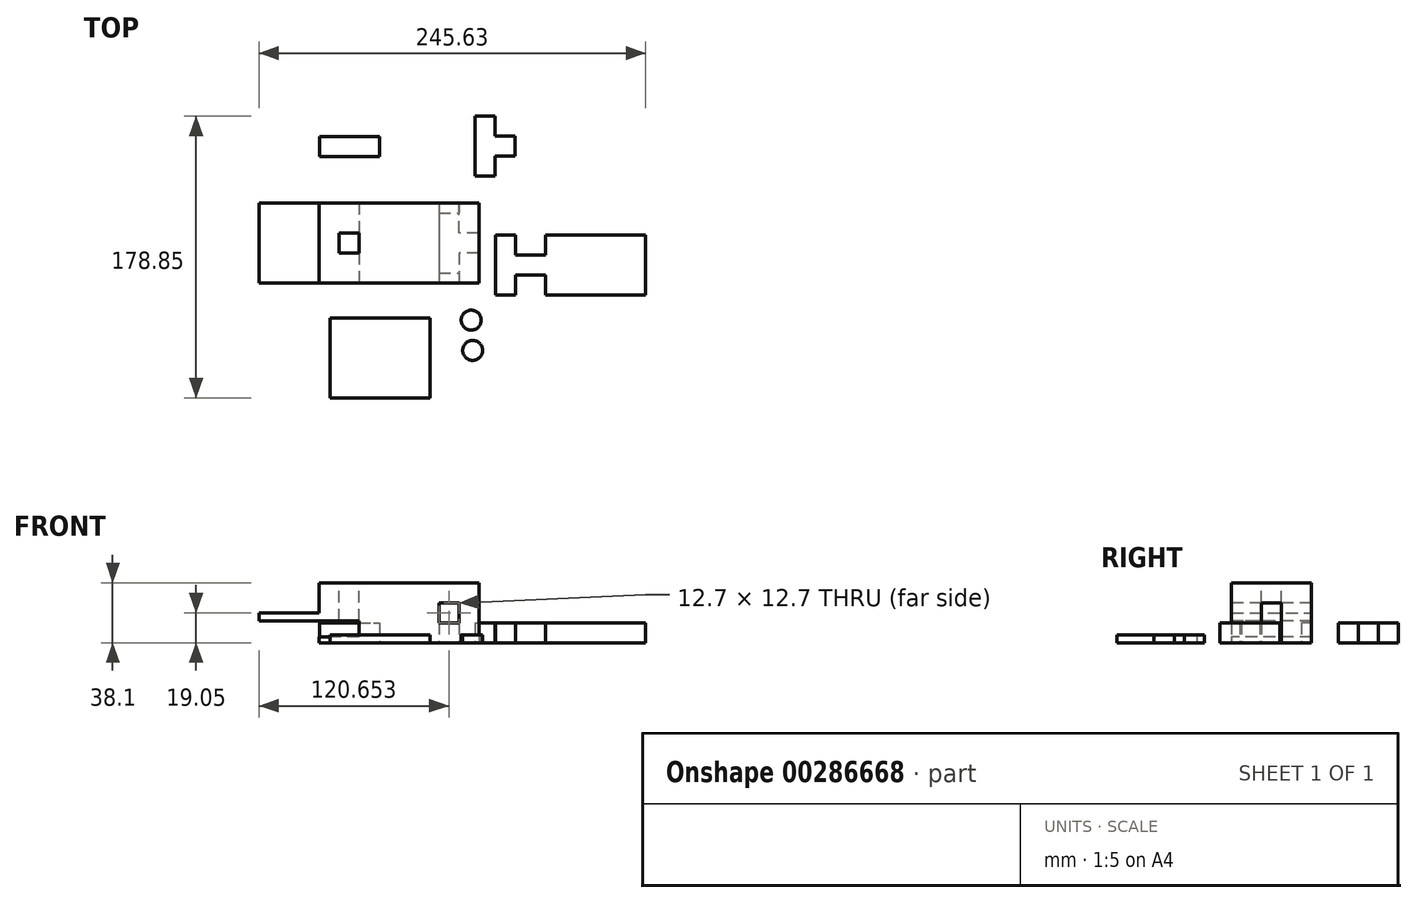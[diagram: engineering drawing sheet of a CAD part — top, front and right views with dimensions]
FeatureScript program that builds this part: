
annotation { "Feature Type Name" : "Feature", "Feature Type Description" : "" }
export const myFeature = defineFeature(function(context is Context, id is Id, definition is map)
    precondition{}
    {
        {
            var Q0;
            Q0=qCreatedBy(makeId("Top.planeOp"),FACE);
            var sketch = newSketch(context, id + "F0", { "sketchPlane" : qUnion([Q0])});
            skLineSegment(sketch, "E0", {"start": v(-57.42, 32.96) * mm, "end": v(44.18, 32.96) * mm});
            skLineSegment(sketch, "E1", {"start": v(-57.42, 32.96) * mm, "end": v(-57.42, -17.84) * mm});
            skLineSegment(sketch, "E2", {"start": v(-57.42, -17.84) * mm, "end": v(44.18, -17.84) * mm});
            skLineSegment(sketch, "E3", {"start": v(44.18, -17.84) * mm, "end": v(44.18, 32.96) * mm});
            skSolve(sketch);
        }
        {
            var Q0;
            Q0=makeQuery(id+"F0.imprint","IMPRINT",FACE,{"disambiguationData":[TD([[makeQuery(id+"F0.imprint","IMPRINT",EDGE,{"derivedFrom":sQuery(id+"F0.wireOp",EDGE,"E0")}),-1.0]])]});
            extrude(context, id + "F1", {"entities" : qUnion([Q0]), "depth" : 38.1 * mm});
        }
        {
            var Q0;
            Q0=makeQuery(id+"F1.opExtrude","SWEPT_FACE",FACE,{"disambiguationData":[OSD([sQuery(id+"F0.wireOp",EDGE,"E1")])]});
            var sketch = newSketch(context, id + "F2", { "sketchPlane" : qUnion([Q0])});
            skLineSegment(sketch, "E4", {"start": v(17.84, 19.05) * mm, "end": v(-32.96, 19.05) * mm});
            skLineSegment(sketch, "E5", {"start": v(-32.96, 19.05) * mm, "end": v(-32.96, 13.97) * mm});
            skLineSegment(sketch, "E6", {"start": v(-32.96, 13.97) * mm, "end": v(17.84, 13.97) * mm});
            skLineSegment(sketch, "E7", {"start": v(17.84, 19.05) * mm, "end": v(17.84, 13.97) * mm});
            skSolve(sketch);
        }
        {
            var Q0;
            Q0 = qSketchRegion(id + "F2", true);
            extrude(context, id + "F3", {"entities" : qUnion([Q0]), "operationType" : NewBodyOperationType.ADD, "depth" : 38.1 * mm});
        }
        {
            var Q0;
            Q0=makeQuery(id+"F1.opExtrude","CAP_FACE",FACE,{"disambiguationData":[OSD([sQuery(id+"F0.wireOp",EDGE,"E0"),sQuery(id+"F0.wireOp",EDGE,"E1"),sQuery(id+"F0.wireOp",EDGE,"E2"),sQuery(id+"F0.wireOp",EDGE,"E3")])],"isStart":true});
            var sketch = newSketch(context, id + "F4", { "sketchPlane" : qUnion([Q0])});
            skLineSegment(sketch, "E8", {"start": v(44.18, 17.84) * mm, "end": v(44.18, -1.2) * mm});
            skLineSegment(sketch, "E9", {"start": v(44.18, -32.96) * mm, "end": v(44.18, -13.9) * mm});
            skLineSegment(sketch, "E10", {"start": v(18.78, -1.2) * mm, "end": v(18.78, -13.9) * mm});
            skLineSegment(sketch, "E11", {"start": v(44.18, -1.2) * mm, "end": v(44.18, -13.9) * mm});
            skLineSegment(sketch, "E12", {"start": v(44.18, -1.2) * mm, "end": v(31.48, -1.2) * mm});
            skLineSegment(sketch, "E13", {"start": v(44.18, -13.9) * mm, "end": v(31.48, -13.9) * mm});
            skLineSegment(sketch, "E14", {"start": v(18.78, -13.9) * mm, "end": v(18.78, -26.6) * mm});
            skLineSegment(sketch, "E15", {"start": v(31.48, -13.9) * mm, "end": v(31.48, -26.6) * mm});
            skLineSegment(sketch, "E16", {"start": v(18.78, -26.6) * mm, "end": v(31.48, -26.6) * mm});
            skLineSegment(sketch, "E17", {"start": v(18.78, -1.2) * mm, "end": v(18.78, 11.5) * mm});
            skLineSegment(sketch, "E18", {"start": v(31.48, -1.2) * mm, "end": v(31.48, 11.5) * mm});
            skLineSegment(sketch, "E19", {"start": v(18.78, 11.5) * mm, "end": v(31.48, 11.5) * mm});
            skLineSegment(sketch, "E20", {"start": v(31.48, -1.2) * mm, "end": v(44.18, -1.2) * mm});
            skLineSegment(sketch, "E21", {"start": v(31.48, -13.9) * mm, "end": v(44.18, -13.9) * mm});
            skSolve(sketch);
        }
        {
            var Q0;
            Q0=makeQuery(id+"F4.imprint","IMPRINT",FACE,{"disambiguationData":[TD([[makeQuery(id+"F4.imprint","IMPRINT",EDGE,{"derivedFrom":sQuery(id+"F4.wireOp",EDGE,"E10")}),1.0]])]});
            extrude(context, id + "F5", {"entities" : qUnion([Q0]), "operationType" : NewBodyOperationType.REMOVE, "oppositeDirection" : true, "depth" : 25.4 * mm});
        }
        {
            var Q0;
            Q0=makeQuery(id+"F3.boolean.opBoolean","MERGE",FACE,{"derivedFrom":[makeQuery(id+"F1.opExtrude","SWEPT_FACE",FACE,{"disambiguationData":[OSD([sQuery(id+"F0.wireOp",EDGE,"E2")])]}),makeQuery(id+"F3.opExtrude","SWEPT_FACE",FACE,{"disambiguationData":[OSD([sQuery(id+"F2.wireOp",EDGE,"E7")])]})]});
            var sketch = newSketch(context, id + "F6", { "sketchPlane" : qUnion([Q0])});
            skLineSegment(sketch, "E22", {"start": v(44.18, 0) * mm, "end": v(31.48, 0) * mm});
            skLineSegment(sketch, "E23", {"start": v(31.48, 25.4) * mm, "end": v(18.78, 25.4) * mm});
            skLineSegment(sketch, "E24", {"start": v(18.78, 25.4) * mm, "end": v(18.78, 12.7) * mm});
            skLineSegment(sketch, "E25", {"start": v(18.78, 12.7) * mm, "end": v(31.48, 12.7) * mm});
            skLineSegment(sketch, "E26", {"start": v(31.48, 25.4) * mm, "end": v(31.48, 12.7) * mm});
            skSolve(sketch);
        }
        {
            var Q0;
            Q0 = qSketchRegion(id + "F6", true);
            extrude(context, id + "F7", {"entities" : qUnion([Q0]), "operationType" : NewBodyOperationType.REMOVE, "oppositeDirection" : true, "depth" : 254 * mm});
        }
        {
            var Q0;
            Q0=makeQuery(id+"F1.opExtrude","CAP_FACE",FACE,{"disambiguationData":[OSD([sQuery(id+"F0.wireOp",EDGE,"E0"),sQuery(id+"F0.wireOp",EDGE,"E1"),sQuery(id+"F0.wireOp",EDGE,"E2"),sQuery(id+"F0.wireOp",EDGE,"E3")])],"isStart":false});
            var sketch = newSketch(context, id + "F8", { "sketchPlane" : qUnion([Q0])});
            skLineSegment(sketch, "E27", {"start": v(-57.42, 32.96) * mm, "end": v(-57.42, -17.84) * mm});
            skLineSegment(sketch, "E28", {"start": v(-44.72, 7.56) * mm, "end": v(-44.72, 13.9) * mm});
            skLineSegment(sketch, "E29", {"start": v(-44.72, 7.56) * mm, "end": v(-44.72, 1.2) * mm});
            skLineSegment(sketch, "E30", {"start": v(-44.72, 1.2) * mm, "end": v(-32.02, 1.2) * mm});
            skLineSegment(sketch, "E31", {"start": v(-32.02, 1.2) * mm, "end": v(-32.02, 13.9) * mm});
            skLineSegment(sketch, "E32", {"start": v(-32.02, 13.9) * mm, "end": v(-44.72, 13.9) * mm});
            skSolve(sketch);
        }
        {
            var Q0;
            Q0=makeQuery(id+"F8.imprint","IMPRINT",FACE,{"disambiguationData":[TD([[makeQuery(id+"F8.imprint","IMPRINT",EDGE,{"derivedFrom":sQuery(id+"F8.wireOp",EDGE,"E28")}),-1.0]])]});
            extrude(context, id + "F9", {"entities" : qUnion([Q0]), "operationType" : NewBodyOperationType.REMOVE, "oppositeDirection" : true, "depth" : 31.75 * mm});
        }
        {
            var Q0;
            {var subQ1=sQuery(id+"F0.wireOp",EDGE,"E1");Q0=makeQuery(id+"F3.boolean.opBoolean","SPLIT",FACE,{"disambiguationData":[TD([makeQuery(id+"F3.opExtrude","SWEPT_FACE",FACE,{"disambiguationData":[OSD([sQuery(id+"F2.wireOp",EDGE,"E6")])]})])],"derivedFrom":makeQuery(id+"F1.opExtrude","SWEPT_FACE",FACE,{"disambiguationData":[OSD([subQ1])]})});}
            var sketch = newSketch(context, id + "F10", { "sketchPlane" : qUnion([Q0])});
            skLineSegment(sketch, "E33", {"start": v(17.84, 13.97) * mm, "end": v(17.84, 3.81) * mm});
            skLineSegment(sketch, "E34", {"start": v(-32.96, 13.97) * mm, "end": v(-32.96, 3.81) * mm});
            skLineSegment(sketch, "E35", {"start": v(-32.96, 3.81) * mm, "end": v(17.84, 3.81) * mm});
            skLineSegment(sketch, "E36", {"start": v(-32.96, 13.97) * mm, "end": v(17.84, 13.97) * mm});
            skSolve(sketch);
        }
        {
            var Q0;
            Q0=makeQuery(id+"F10.imprint","IMPRINT",FACE,{"disambiguationData":[TD([[makeQuery(id+"F10.imprint","IMPRINT",EDGE,{"derivedFrom":sQuery(id+"F10.wireOp",EDGE,"E33")}),-1.0]])]});
            extrude(context, id + "F11", {"entities" : qUnion([Q0]), "operationType" : NewBodyOperationType.REMOVE, "oppositeDirection" : true, "depth" : 25.4 * mm});
        }
        {
            var Q0;
            Q0=qCreatedBy(makeId("Top.planeOp"),FACE);
            var sketch = newSketch(context, id + "F12", { "sketchPlane" : qUnion([Q0])});
            skLineSegment(sketch, "E37", {"start": v(-57.14, 75.1) * mm, "end": v(-57.14, 62.4) * mm});
            skLineSegment(sketch, "E38", {"start": v(-57.14, 75.1) * mm, "end": v(-19.04, 75.1) * mm});
            skLineSegment(sketch, "E39", {"start": v(-19.04, 75.1) * mm, "end": v(-19.04, 62.4) * mm});
            skLineSegment(sketch, "E40", {"start": v(-57.14, 62.4) * mm, "end": v(-19.04, 62.4) * mm});
            skSolve(sketch);
        }
        {
            var Q0;
            Q0=makeQuery(id+"F12.imprint","IMPRINT",FACE,{"disambiguationData":[TD([[makeQuery(id+"F12.imprint","IMPRINT",EDGE,{"derivedFrom":sQuery(id+"F12.wireOp",EDGE,"E37")}),1.0]])]});
            extrude(context, id + "F13", {"entities" : qUnion([Q0]), "depth" : 12.7 * mm});
        }
        {
            var Q0;
            Q0=qCreatedBy(makeId("Top.planeOp"),FACE);
            var sketch = newSketch(context, id + "F14", { "sketchPlane" : qUnion([Q0])});
            skLineSegment(sketch, "E41", {"start": v(-50.48, -39.98) * mm, "end": v(-50.48, -90.78) * mm});
            skLineSegment(sketch, "E42", {"start": v(-50.48, -39.98) * mm, "end": v(13.02, -39.98) * mm});
            skLineSegment(sketch, "E43", {"start": v(-50.48, -90.78) * mm, "end": v(13.02, -90.78) * mm});
            skLineSegment(sketch, "E44", {"start": v(13.02, -39.98) * mm, "end": v(13.02, -90.78) * mm});
            skSolve(sketch);
        }
        {
            var Q0;
            Q0=makeQuery(id+"F14.imprint","IMPRINT",FACE,{"disambiguationData":[TD([[makeQuery(id+"F14.imprint","IMPRINT",EDGE,{"derivedFrom":sQuery(id+"F14.wireOp",EDGE,"E41")}),1.0]])]});
            extrude(context, id + "F15", {"entities" : qUnion([Q0]), "depth" : 5.08 * mm});
        }
        {
            var Q0;
            Q0=qCreatedBy(makeId("Top.planeOp"),FACE);
            var sketch = newSketch(context, id + "F16", { "sketchPlane" : qUnion([Q0])});
            skLineSegment(sketch, "E45", {"start": v(54.86, -25.4) * mm, "end": v(67.56, -25.4) * mm});
            skLineSegment(sketch, "E46", {"start": v(54.86, -25.4) * mm, "end": v(54.86, 12.7) * mm});
            skLineSegment(sketch, "E47", {"start": v(54.86, 12.7) * mm, "end": v(67.56, 12.7) * mm});
            skLineSegment(sketch, "E48", {"start": v(67.56, 12.7) * mm, "end": v(67.56, 0) * mm});
            skLineSegment(sketch, "E49", {"start": v(67.56, -25.4) * mm, "end": v(67.56, -12.7) * mm});
            skLineSegment(sketch, "E50", {"start": v(67.56, -12.7) * mm, "end": v(86.6, -12.7) * mm});
            skLineSegment(sketch, "E51", {"start": v(67.56, 0) * mm, "end": v(86.6, 0) * mm});
            skLineSegment(sketch, "E52", {"start": v(86.6, 0) * mm, "end": v(86.6, 12.7) * mm});
            skLineSegment(sketch, "E53", {"start": v(86.6, -12.7) * mm, "end": v(86.6, -25.4) * mm});
            skLineSegment(sketch, "E54", {"start": v(86.6, -25.4) * mm, "end": v(150.1, -25.4) * mm});
            skLineSegment(sketch, "E55", {"start": v(150.1, -25.4) * mm, "end": v(150.1, 12.7) * mm});
            skLineSegment(sketch, "E56", {"start": v(86.6, 12.7) * mm, "end": v(150.1, 12.7) * mm});
            skSolve(sketch);
        }
        {
            var Q0;
            Q0 = qSketchRegion(id + "F16", true);
            extrude(context, id + "F17", {"entities" : qUnion([Q0]), "depth" : 12.7 * mm});
        }
        {
            var Q0;
            Q0=qCreatedBy(makeId("Top.planeOp"),FACE);
            var sketch = newSketch(context, id + "F18", { "sketchPlane" : qUnion([Q0])});
            skLineSegment(sketch, "E57", {"start": v(41.59, 88.07) * mm, "end": v(41.59, 49.97) * mm});
            skLineSegment(sketch, "E58", {"start": v(41.59, 49.97) * mm, "end": v(54.29, 49.97) * mm});
            skLineSegment(sketch, "E59", {"start": v(41.59, 88.07) * mm, "end": v(54.29, 88.07) * mm});
            skLineSegment(sketch, "E60", {"start": v(54.29, 88.07) * mm, "end": v(54.29, 75.37) * mm});
            skLineSegment(sketch, "E61", {"start": v(54.29, 49.97) * mm, "end": v(54.29, 62.67) * mm});
            skLineSegment(sketch, "E62", {"start": v(54.29, 62.67) * mm, "end": v(66.99, 62.67) * mm});
            skLineSegment(sketch, "E63", {"start": v(54.29, 75.37) * mm, "end": v(66.99, 75.37) * mm});
            skLineSegment(sketch, "E64", {"start": v(66.99, 75.37) * mm, "end": v(66.99, 62.67) * mm});
            skSolve(sketch);
        }
        {
            var Q0;
            Q0 = qSketchRegion(id + "F18", true);
            extrude(context, id + "F19", {"entities" : qUnion([Q0]), "depth" : 12.7 * mm});
        }
        {
            var Q0;
            Q0=qCreatedBy(makeId("Top.planeOp"),FACE);
            var sketch = newSketch(context, id + "F20", { "sketchPlane" : qUnion([Q0])});
            skCircle(sketch, "E65", {"center": v(39.31, -41.46) * mm, "radius": 6.35 * mm});
            skCircle(sketch, "E66", {"center": v(40.2, -60.69) * mm, "radius": 6.35 * mm});
            skSolve(sketch);
        }
        {
            var Q0;
            Q0 = qSketchRegion(id + "F20", true);
            extrude(context, id + "F21", {"entities" : qUnion([Q0]), "depth" : 5.08 * mm});
        }
    });
